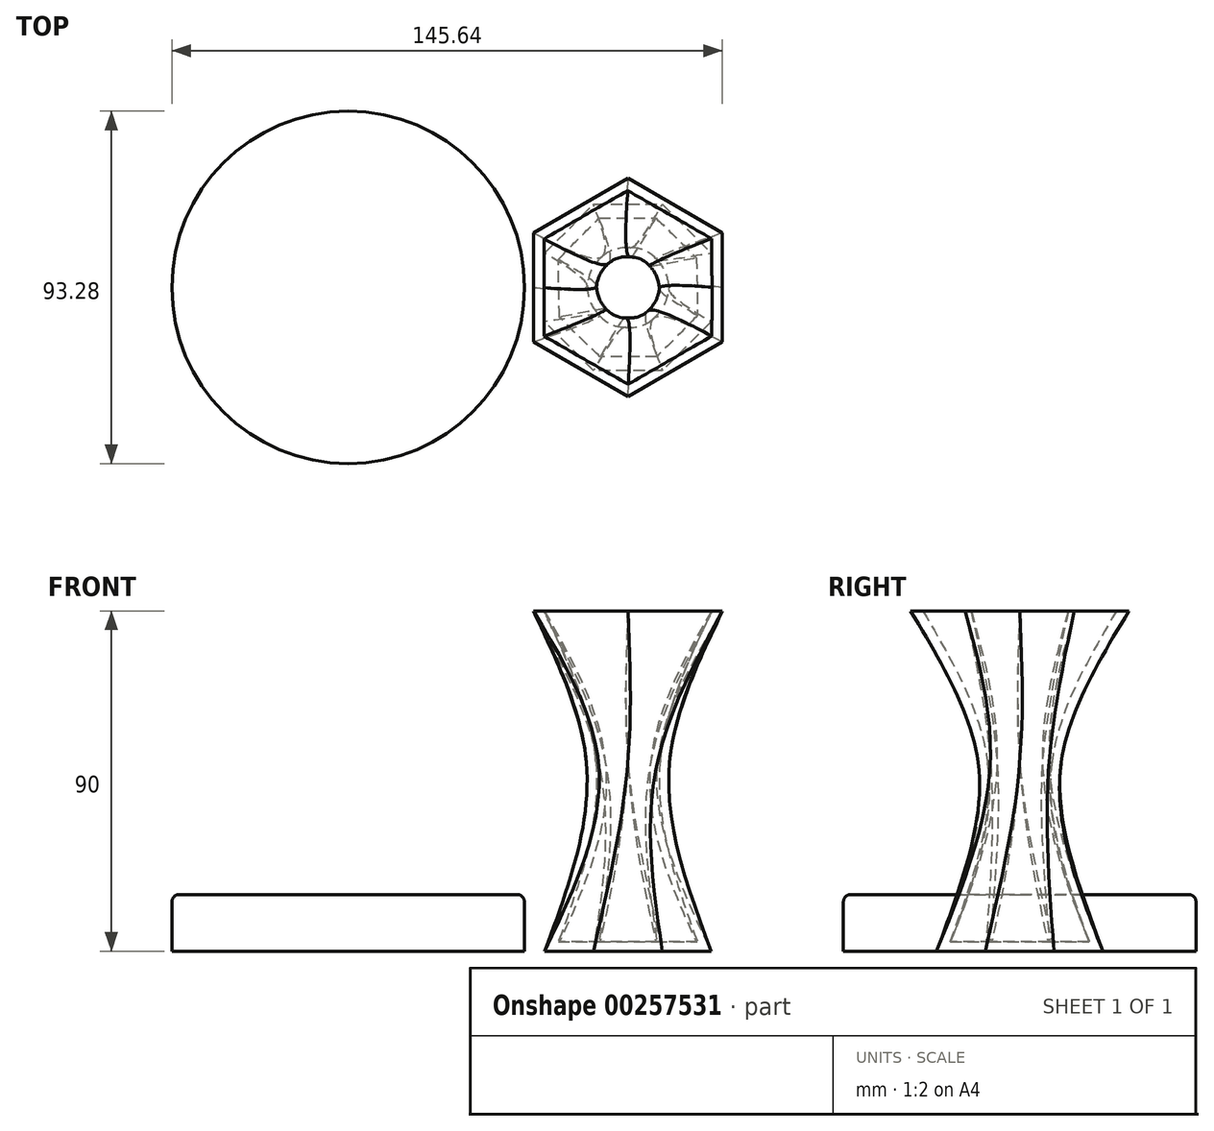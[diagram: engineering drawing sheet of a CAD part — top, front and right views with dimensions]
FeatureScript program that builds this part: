
annotation { "Feature Type Name" : "Feature", "Feature Type Description" : "" }
export const myFeature = defineFeature(function(context is Context, id is Id, definition is map)
    precondition{}
    {
        {
            var Q0;
            Q0=qCreatedBy(makeId("Top.planeOp"),FACE);
            var sketch = newSketch(context, id + "F0", { "sketchPlane" : qUnion([Q0])});
            skCircle(sketch, "E0.cCircle", {"center": v(0, 0) * mm, "radius": 25 * mm, "construction": true});
            skLineSegment(sketch, "E0.0", {"start": v(0, 28.87) * mm, "end": v(25, 14.43) * mm});
            skLineSegment(sketch, "E0.1", {"start": v(25, 14.43) * mm, "end": v(25, -14.43) * mm});
            skLineSegment(sketch, "E0.2", {"start": v(25, -14.43) * mm, "end": v(0, -28.87) * mm});
            skLineSegment(sketch, "E0.3", {"start": v(0, -28.87) * mm, "end": v(-25, -14.43) * mm});
            skLineSegment(sketch, "E0.4", {"start": v(-25, -14.43) * mm, "end": v(-25, 14.43) * mm});
            skLineSegment(sketch, "E0.5", {"start": v(-25, 14.43) * mm, "end": v(0, 28.87) * mm});
            skPoint(sketch, "E0.0.midPoint", {"position": v(12.5, 21.65) * mm});
            skSolve(sketch);
        }
        {
            var Q0;
            Q0=qCreatedBy(makeId("Top.planeOp"),FACE);
            cPlane(context, id + "F1", {"entities" : qUnion([Q0]), "cplaneType" : CPlaneType.OFFSET, "offset" : 40 * mm, "oppositeDirection" : true, "width" : 150 * mm, "height" : 150 * mm});
        }
        {
            var Q0;
            Q0=qCreatedBy(id+"F1.planeOp",FACE);
            var sketch = newSketch(context, id + "F2", { "sketchPlane" : qUnion([Q0])});
            skCircle(sketch, "E1", {"center": v(0, 0) * mm, "radius": 11 * mm});
            skSolve(sketch);
        }
        {
            var Q0;
            Q0=qCreatedBy(id+"F1.planeOp",FACE);
            cPlane(context, id + "F3", {"entities" : qUnion([Q0]), "cplaneType" : CPlaneType.OFFSET, "offset" : 50 * mm, "oppositeDirection" : true, "width" : 150 * mm, "height" : 150 * mm});
        }
        {
            var Q0;
            Q0=qCreatedBy(id+"F3.planeOp",FACE);
            var sketch = newSketch(context, id + "F4", { "sketchPlane" : qUnion([Q0])});
            skCircle(sketch, "E2.cCircle", {"center": v(0, 0) * mm, "radius": 22 * mm, "construction": true});
            skLineSegment(sketch, "E2.0", {"start": v(22, 9.1) * mm, "end": v(22, -9.1) * mm});
            skLineSegment(sketch, "E2.1", {"start": v(22, -9.1) * mm, "end": v(9.1, -22) * mm});
            skLineSegment(sketch, "E2.2", {"start": v(9.1, -22) * mm, "end": v(-9.1, -22) * mm});
            skLineSegment(sketch, "E2.3", {"start": v(-9.1, -22) * mm, "end": v(-22, -9.1) * mm});
            skLineSegment(sketch, "E2.4", {"start": v(-22, -9.1) * mm, "end": v(-22, 9.1) * mm});
            skLineSegment(sketch, "E2.5", {"start": v(-22, 9.1) * mm, "end": v(-9.1, 22) * mm});
            skLineSegment(sketch, "E2.6", {"start": v(-9.1, 22) * mm, "end": v(9.1, 22) * mm});
            skLineSegment(sketch, "E2.7", {"start": v(9.1, 22) * mm, "end": v(22, 9.1) * mm});
            skPoint(sketch, "E2.0.midPoint", {"position": v(22, 0) * mm});
            skSolve(sketch);
        }
        {
            var Q0;
            Q0=makeQuery(id+"F0.imprint","IMPRINT",FACE,{"disambiguationData":[TD([[makeQuery(id+"F0.imprint","IMPRINT",EDGE,{"derivedFrom":sQuery(id+"F0.wireOp",EDGE,"E0.0")}),-1.0]])]});
            var Q1;
            Q1=makeQuery(id+"F2.imprint","IMPRINT",FACE,{"disambiguationData":[TD([[makeQuery(id+"F2.imprint","IMPRINT",EDGE,{"derivedFrom":sQuery(id+"F2.wireOp",EDGE,"E1")}),1.0]])]});
            var Q2;
            Q2=makeQuery(id+"F4.imprint","IMPRINT",FACE,{"disambiguationData":[TD([[makeQuery(id+"F4.imprint","IMPRINT",EDGE,{"derivedFrom":sQuery(id+"F4.wireOp",EDGE,"E2.0")}),-1.0]])]});
            loft(context, id + "F5", {"sheetProfilesArray" : [{ "sheetProfileEntities" : qUnion([Q0]) }, { "sheetProfileEntities" : qUnion([Q1]) }, { "sheetProfileEntities" : qUnion([Q2]) }]});
        }
        {
            var Q0;
            Q0=makeQuery(id+"F5.opLoft","CAP_FACE",FACE,{"disambiguationData":[OSD([makeQuery(id+"F0.imprint","IMPRINT",FACE,{"disambiguationData":[TD([[makeQuery(id+"F0.imprint","IMPRINT",EDGE,{"derivedFrom":sQuery(id+"F0.wireOp",EDGE,"E0.0")}),-1.0]])]})])],"isStart":true});
            shell(context, id + "F6", {"entities" : qUnion([Q0]), "thickness" : 2.5 * mm});
        }
        {
            var Q0;
            Q0=qCreatedBy(id+"F3.planeOp",FACE);
            var sketch = newSketch(context, id + "F7", { "sketchPlane" : qUnion([Q0])});
            skCircle(sketch, "E3", {"center": v(-74, 0) * mm, "radius": 46.64 * mm});
            skSolve(sketch);
        }
        {
            var Q0;
            Q0 = qSketchRegion(id + "F7", true);
            extrude(context, id + "F8", {"entities" : qUnion([Q0]), "depth" : 15 * mm});
        }
        {
            var Q0;
            Q0=makeQuery(id+"F8.opExtrude","CAP_EDGE",EDGE,{"disambiguationData":[OSD([sQuery(id+"F7.wireOp",EDGE,"E3")])],"isStart":false});
            fillet(context, id + "F9", {"entities" : qUnion([Q0]), "radius" : 2 * mm, "tangentPropagation" : true, "allowEdgeOverflow" : false});
        }
    });
